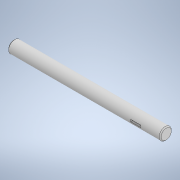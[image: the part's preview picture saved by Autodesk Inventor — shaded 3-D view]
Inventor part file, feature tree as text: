
AUTODESK INVENTOR PART (.ipt)
format: ipt  version: 2021 (Build 250183000, 183)  size: 138,240 bytes
history: native  units: mm
features: other x6, sketch x2, chamfer x1, extrude x1
ambient origin geometry x8: Origin, YZ Plane, XZ Plane, XY Plane, X Axis, Y Axis, Z Axis, Center Point
bodies: Body1 (feature_tree)
feature tree (10):
  other  "Sólido1"
  other  "Revolução1"
  sketch  "Esboço2"  dims[d1=3.0mm d2=90.0deg d3=0.5mm d4=2.0mm d5=45.0deg d6=5.0mm d9=5.0mm d10=12.0mm d11=1.5mm d12=12.0mm d13=1.5mm d14=1.0mm d15=0.0mm d17=2.5mm d19=5.0mm d20=3.0mm d21=1.0mm d16=0.5mm d18=0.5mm]
  chamfer  "Chanfro1"  Angle=90.0deg  [1 undecoded]
  extrude  "Extrusão1"  Depth=1.0mm TaperAngle=45.0deg
  sketch  "Esboço1"  dims[d0=75.0mm]
  other  "Contorno projetado1"
  other  "Projetar arestas de corte1"
  other  "Projetar arestas de corte2"
  other  "Projetar arestas de corte3"
note: 1 required parameter value undecoded (feature->parameter linkage not recoverable at this tier; creation-order binding heuristic only, values carry confidence <= 0.55)
